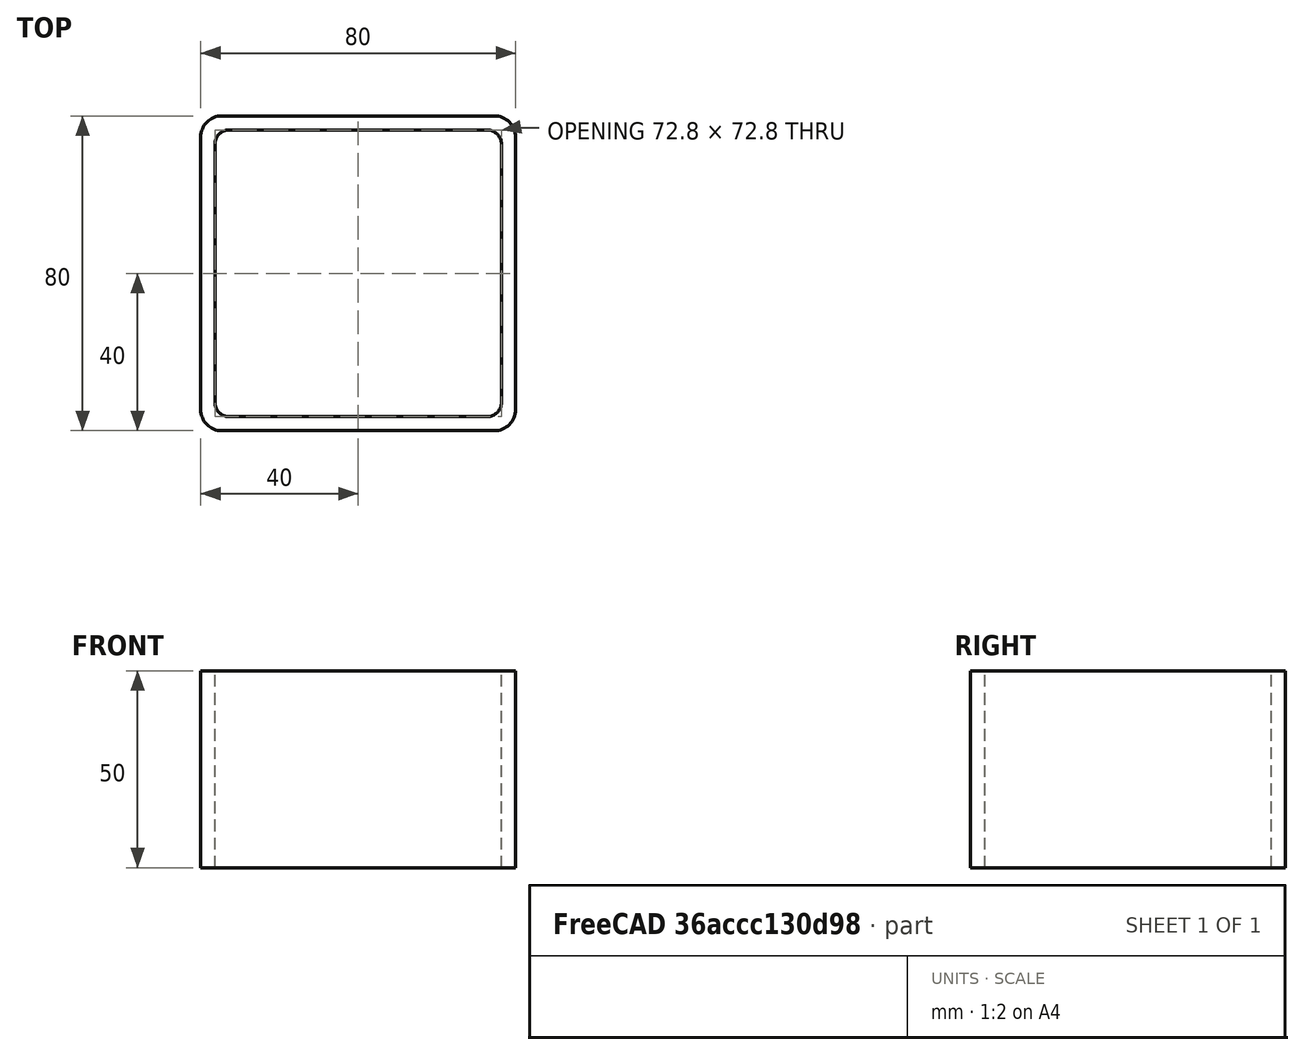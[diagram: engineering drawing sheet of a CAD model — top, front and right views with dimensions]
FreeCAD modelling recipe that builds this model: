
FCSTD DOCUMENT  (FreeCAD 0.15R4671 (Git))
Label: Square hollow section 80x80x3.6 EN10219 S235JRH
License: All rights reserved
LicenseURL: http://en.wikipedia.org/wiki/All_rights_reserved
objects: Sketcher::SketchObject×1, Part::Extrusion×1
note: 2 computed .brp shape members not serialized (recipe doc carries the construction recipe); baked Part::Feature solids carry a one-line shape summary decoded from their .brp

FEATURE [Sketcher::SketchObject] Sketch
  sketch-geometry (16):
    g0: LineSegment StartX=-32.8 StartY=36.4 StartZ=0 EndX=32.8 EndY=36.4 EndZ=0
    g1: LineSegment StartX=36.4 StartY=32.8 StartZ=0 EndX=36.4 EndY=-32.8 EndZ=0
    g2: LineSegment StartX=32.8 StartY=-36.4 StartZ=0 EndX=-32.8 EndY=-36.4 EndZ=0
    g3: LineSegment StartX=-36.4 StartY=-32.8 StartZ=0 EndX=-36.4 EndY=32.8 EndZ=0
    g4: LineSegment StartX=-34.6 StartY=40 StartZ=0 EndX=34.6 EndY=40 EndZ=0
    g5: LineSegment StartX=40 StartY=34.6 StartZ=0 EndX=40 EndY=-34.6 EndZ=0
    g6: LineSegment StartX=34.6 StartY=-40 StartZ=0 EndX=-34.6 EndY=-40 EndZ=0
    g7: LineSegment StartX=-40 StartY=-34.6 StartZ=0 EndX=-40 EndY=34.6 EndZ=0
    g8: ArcOfCircle CenterX=-32.8 CenterY=32.8 CenterZ=0 NormalX=0 NormalY=0 NormalZ=1 Radius=3.6 StartAngle=1.5708 EndAngle=3.14159
    g9: ArcOfCircle CenterX=32.8 CenterY=32.8 CenterZ=0 NormalX=0 NormalY=0 NormalZ=1 Radius=3.6 StartAngle=0 EndAngle=1.5708
    g10: ArcOfCircle CenterX=32.8 CenterY=-32.8 CenterZ=0 NormalX=0 NormalY=0 NormalZ=1 Radius=3.6 StartAngle=4.71239 EndAngle=6.28319
    g11: ArcOfCircle CenterX=-32.8 CenterY=-32.8 CenterZ=0 NormalX=0 NormalY=0 NormalZ=1 Radius=3.6 StartAngle=3.14159 EndAngle=4.71239
    g12: ArcOfCircle CenterX=34.6 CenterY=34.6 CenterZ=0 NormalX=0 NormalY=0 NormalZ=1 Radius=5.4 StartAngle=0 EndAngle=1.5708
    g13: ArcOfCircle CenterX=34.6 CenterY=-34.6 CenterZ=0 NormalX=0 NormalY=0 NormalZ=1 Radius=5.4 StartAngle=4.71239 EndAngle=6.28319
    g14: ArcOfCircle CenterX=-34.6 CenterY=-34.6 CenterZ=0 NormalX=0 NormalY=0 NormalZ=1 Radius=5.4 StartAngle=3.14159 EndAngle=4.71239
    g15: ArcOfCircle CenterX=-34.6 CenterY=34.6 CenterZ=0 NormalX=0 NormalY=0 NormalZ=1 Radius=5.4 StartAngle=1.5708 EndAngle=3.14159
  constraints (36):
    c: Horizontal(g2)
    c: Vertical(g3)
    c: Horizontal(g6)
    c: Vertical(g7)
    c: Tangent(g3,g8) = 1.5708
    c: Tangent(g0,g8) = 1.5708
    c: Tangent(g0,g9) = 1.5708
    c: Tangent(g1,g9) = 1.5708
    c: Tangent(g1,g10) = 1.5708
    c: Tangent(g2,g10) = 1.5708
    c: Tangent(g2,g11) = 1.5708
    c: Tangent(g3,g11) = 1.5708
    c: Tangent(g4,g12) = 1.5708
    c: Tangent(g5,g12) = 1.5708
    c: Tangent(g5,g13) = 1.5708
    c: Tangent(g6,g13) = 1.5708
    c: Tangent(g6,g14) = 1.5708
    c: Tangent(g7,g14) = 1.5708
    c: Tangent(g7,g15) = 1.5708
    c: Tangent(g4,g15) = 1.5708
    c: Equal(g9,g8)
    c: Equal(g9,g11)
    c: Equal(g9,g10)
    c: Equal(g12,g15)
    c: Equal(g12,g14)
    c: Equal(g12,g13)
    c: Symmetric(g4,g6,g-1)
    c: Symmetric(g7,g5,g-2)
    c: DistanceY(g4,g6) = -80
    c: DistanceX(g7,g5) = 80
    c: Symmetric(g3,g1,g-2)
    c: Symmetric(g0,g2,g-1)
    c: DistanceY(g0,g4) = 3.6
    c: DistanceX(g5,g1) = -3.6
    c: Radius(g9) = 3.6
    c: Radius(g12) = 5.4
FEATURE [Part::Extrusion] Extrude  label="Square hollow section 80x80x3.6 EN10219 S235JRH"
  Base = -> Sketch
  Dir = (0,0,50)
  Solid = true
